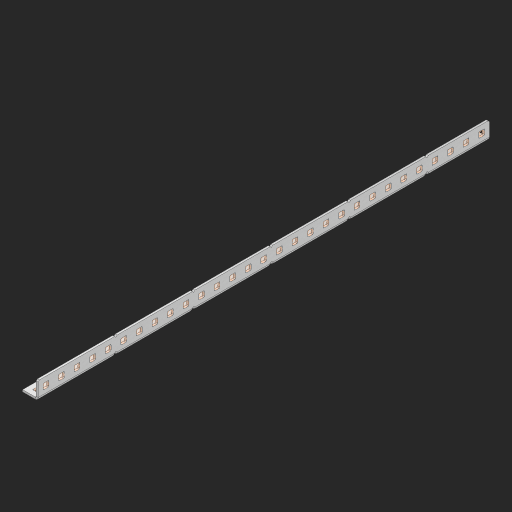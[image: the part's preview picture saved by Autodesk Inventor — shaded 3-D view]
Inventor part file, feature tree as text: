
AUTODESK INVENTOR PART (.ipt)
format: ipt  version: 2023 (Build 270158000, 158)  size: 939,008 bytes
history: native  units: in
note: dims shown in document units (in); Inventor stores cm internally (conversion verified against a paired STEP export)
features: other x63, extrude x57, sheet_metal_op x10, sketch x8, mirror x1, pattern_linear x1, chamfer x1
ambient origin geometry x8: Origin, YZ Plane, XZ Plane, XY Plane, X Axis, Y Axis, Z Axis, Center Point
bodies: Solid1 (feature_tree), Body (feature_tree)
feature tree (141):
  other  "Flange Pattern Plane"
  sheet_metal_op  "Flange Pattern"
  sheet_metal_op  "Body Pattern"
  other  "Arc Length"
  mirror  "Notch Mirror"
  pattern_linear  "Notch Pattern"  Spacing1=0.25in  [1 undecoded]
  chamfer  "End Chamfer"
  extrude  "Half Cut"  Depth=0.0625in
  sketch  "Sketch1"  dims[d0=1.5in]
  other  "Plate1"
  sketch  "Sketch2"  dims[d1=14.5in]
  other  "Plate2"
  sheet_metal_op  "Bend1"
  sheet_metal_op  "Corner1"
  sketch  "Sketch3"  dims[d2=0.0625in]
  other  "Flange Pattern Sketch"
  sketch  "Sketch7"  dims[d3=0.0625in]
  other  "Srf1"
  other  "Srf2"
  sketch  "Sketch8"  dims[d4=0.0312in]
  sketch  "Sketch9"  dims[d5=0.125in]
  other  "Srf91"
  sheet_metal_op  "Body Pattern Sketch"
  other  "Srf92"
  sketch  "Sketch13"  dims[d6=0.0625in]
  sketch  "Sketch14"  dims[d7=0.5in d8=90.0deg d9=0.0312in d10=0.25in d11=0.0625in d12=0.0625in d16=0.182in d17=0.02in d18=0.0625in d19=0.0in d20=0.25in d21=0.25in d46=0.172in d47=1.0in d48=0.0in d49=0.182in d50=0.02in d51=0.25in d52=0.25in d53=0.0625in d54=0.0in d55=0.172in d56=1.0in d57=0.0in d60=11.4173in d62=0.5in d63=0.3937in d65=0.5in d85=0.1473in d86=0.1782in d88=0.04in d89=0.0625in d90=0.0in d91=0.04in d92=0.0491in d95=2.5in d96=0.04in d97=0.25in d98=45.0deg d101=0.0in d102=2.497in d131=0.5in d132=11.4173in d134=0.5in d139=0.5in]
  other  "Srf856"
  other  "Srf1310"
  other  "Srf1311"
  other  "Srf1312"
  other  "Srf1376"
  other  "Srf1377"
  other  "Srf1728"
  other  "Srf1755"
  other  "Srf1878"
  other  "Srf1879"
  other  "Srf1880"
  other  "Srf1881"
  other  "Srf1882"
  other  "Srf1883"
  other  "Srf1884"
  other  "Srf1885"
  other  "Srf1886"
  other  "Srf1887"
  other  "Srf1888"
  other  "Srf1889"
  other  "Srf1890"
  other  "Srf1891"
  other  "Srf1892"
  other  "Srf1893"
  other  "Srf1894"
  other  "Srf1895"
  other  "Srf1896"
  other  "Srf1897"
  other  "Srf1898"
  other  "Srf1899"
  other  "Srf1900"
  other  "Srf1942"
  other  "Srf1943"
  other  "Srf1944"
  other  "Srf1945"
  other  "Srf1946"
  other  "Srf1947"
  other  "Srf1948"
  other  "Srf1949"
  other  "Srf1950"
  other  "Srf1951"
  other  "Srf1952"
  other  "Srf1953"
  other  "Srf1954"
  other  "Srf1955"
  other  "Srf1956"
  other  "Srf1957"
  other  "Srf1958"
  other  "Srf1959"
  other  "Srf1960"
  other  "Srf1961"
  other  "Srf1962"
  other  "Srf1963"
  other  "Srf1964"
  sheet_metal_op  "Flange Stamp"
  sheet_metal_op  "Flange Circle"
  sheet_metal_op  "Body Stamp"
  sheet_metal_op  "Body Circle"
  sheet_metal_op  "Notch"
  extrude  "ExtrusionSrf2"  Depth=0.0625in
  extrude  "ExtrusionSrf92"  Depth=0.5in
  extrude  "ExtrusionSrf856"  Depth=0.02in
  extrude  "ExtrusionSrf1310"  Depth=0.0625in
  extrude  "ExtrusionSrf1311"  TaperAngle=0.0deg  [1 undecoded]
  extrude  "ExtrusionSrf1312"  Depth=0.5in
  extrude  "ExtrusionSrf1376"  Depth=0.5in
  extrude  "ExtrusionSrf1377"  Depth=0.5in
  extrude  "ExtrusionSrf1728"  Depth=0.5in TaperAngle=0.0deg
  extrude  "ExtrusionSrf1755"  Depth=0.5in
  extrude  "ExtrusionSrf1878"  Depth=0.02in
  extrude  "ExtrusionSrf1879"  Depth=0.5in
  extrude  "ExtrusionSrf1880"  Depth=0.5in
  extrude  "ExtrusionSrf1881"  Depth=0.0625in
  extrude  "ExtrusionSrf1882"  TaperAngle=0.0deg  [1 undecoded]
  extrude  "ExtrusionSrf1883"  Depth=0.5in
  extrude  "ExtrusionSrf1884"  Depth=0.5in TaperAngle=0.0deg
  extrude  "ExtrusionSrf1885"  Depth=0.5in
  extrude  "ExtrusionSrf1886"  Depth=0.5in
  extrude  "ExtrusionSrf1887"  Depth=0.5in
  extrude  "ExtrusionSrf1888"  Depth=0.5in
  extrude  "ExtrusionSrf1889"  Depth=0.5in
  extrude  "ExtrusionSrf1890"  Depth=0.0625in
  extrude  "ExtrusionSrf1891"  TaperAngle=0.0deg  [1 undecoded]
  extrude  "ExtrusionSrf1892"  Depth=0.5in
  extrude  "ExtrusionSrf1893"  Depth=0.5in
  extrude  "ExtrusionSrf1894"  Depth=0.5in
  extrude  "ExtrusionSrf1895"  Depth=0.5in TaperAngle=45.0deg
  extrude  "ExtrusionSrf1896"  TaperAngle=0.0deg  [1 undecoded]
  extrude  "ExtrusionSrf1897"  Depth=0.5in
  extrude  "ExtrusionSrf1898"  Depth=0.5in
  extrude  "ExtrusionSrf1899"  Depth=0.5in
  extrude  "ExtrusionSrf1900"  Depth=0.5in
  extrude  "ExtrusionSrf1942"  Depth=0.5in
  extrude  "ExtrusionSrf1943"  [1 undecoded]
  extrude  "ExtrusionSrf1944"  [1 undecoded]
  extrude  "ExtrusionSrf1945"  [1 undecoded]
  extrude  "ExtrusionSrf1946"  [1 undecoded]
  extrude  "ExtrusionSrf1947"  [1 undecoded]
  extrude  "ExtrusionSrf1948"  [1 undecoded]
  extrude  "ExtrusionSrf1949"  [1 undecoded]
  extrude  "ExtrusionSrf1950"  [1 undecoded]
  extrude  "ExtrusionSrf1951"  [1 undecoded]
  extrude  "ExtrusionSrf1952"  [1 undecoded]
  extrude  "ExtrusionSrf1953"  [1 undecoded]
  extrude  "ExtrusionSrf1954"  [1 undecoded]
  extrude  "ExtrusionSrf1955"  [1 undecoded]
  extrude  "ExtrusionSrf1956"  [1 undecoded]
  extrude  "ExtrusionSrf1957"  [1 undecoded]
  extrude  "ExtrusionSrf1958"  [1 undecoded]
  extrude  "ExtrusionSrf1959"  [1 undecoded]
  extrude  "ExtrusionSrf1960"  [1 undecoded]
  extrude  "ExtrusionSrf1961"  [1 undecoded]
  extrude  "ExtrusionSrf1962"  [1 undecoded]
  extrude  "ExtrusionSrf1963"  [1 undecoded]
  extrude  "ExtrusionSrf1964"  [1 undecoded]
note: 27 required parameter values undecoded (feature->parameter linkage not recoverable at this tier; creation-order binding heuristic only, values carry confidence <= 0.55)
